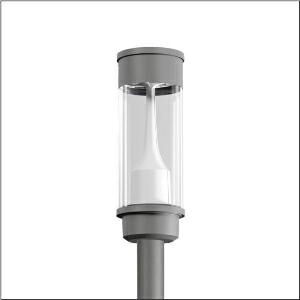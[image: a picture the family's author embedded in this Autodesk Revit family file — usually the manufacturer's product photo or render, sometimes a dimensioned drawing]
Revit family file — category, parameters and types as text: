
# Revit family: litepole_iq___pl1_2s_5xa5415cf14h_d917
name_source: partatom
category: Lighting Fixtures
units: mm (PartAtom-declared; Revit-internal decimal feet)

## family parameters
Cut with Voids When Loaded = No
Host = Face
Light Source = No
Part Type = Normal
Room Calculation Point = No
Round Connector Dimension = Use Diameter
Shared = No

## types (1)
- --- (1 x LED, 2970 lm, 23.9 W, 2200K)
    Apparent Load = 24 VA
    CIE Flux Codes = 23 62 94 96 100
    Color Rendering = 70
    Color Temperature = 2200K
    Default Elevation = 1800 mm
    Description = Litepole iQ, mast luminaire, Module 540 iQ-SR, primary light control with 3 zone facetted reflector, of plastic, silver coated, highly specular, structured, primary optical cover: cover, of PMMA, transparent, partly coated, light distribution: PL1.2s, light emission: direct distribution, primary light characteristic: symmetric, installation type: post-top, LED, High Power LED, rated luminous flux: 2.970lm, luminous efficacy: 124lm/W, light colour: 722, colour temperature: 2200K, control gear: ECG iQ, control: optimised constant luminous flux control (CLO 2.0), Desk-Remote (wireless, voltage-free reading and setting of iQ features in the workshop via application-optimized NFC function/RFID function), Light-Fading, Smart-Wire, Night-Set, Lumen-Switch, Temp-Guard, Auto-Match, Street-Remote, presetting dimming logarithmic, with terminal, 6-pole, max. 2.5mm², mains connection: 230..240V, AC, 50/60Hz, start of lifetime: 24W, end of service life: 26W, reduction: 12W, luminaire housing, upper part, of glass-fibre reinforced polyester, coated, Siteco® metallic grey (DB 702S), diameter: 210mm, height: 590mm, spigot size: d x l = 76 x 70mm (post-top) | with reducer (optional accessory) 60 x 70mm, post-top mast mounting element, of diecast aluminium, coated, Siteco® metallic grey (DB 702S), Module 540 iQ-SR, traffic white (RAL 9016), equipment: standard, protection rating (complete): IP65, insulation class (complete): insulation class II (safety insulation), certification: CE, ENEC, VDE, packaging unit: 1 piece

Light Distribution: PL1.2s
    Height = 590 mm
    Lamp = 1 x LED
    Lamp Light Flux = 2970 lm
    Lamp Power = 23.9 W
    Lamp count = 1
    Length = 220 mm
    Luminous efficacy = 124 lm/W
    Manufacturer = Siteco
    ModVariant = No
    Model = 5XA5415CF14H
    Number of Poles = 1
    OnlyDefault = Yes
    Power Factor = 1
    Product Name = Litepole iQ | PL1.2s
    Product group = mast luminaire | pylon top
    ProductGroupID = 6100
    Protection Class = Protection class II
    Protection Degree = IP 65
    RLX_Detail_Level = 1
    RLX_Emergency_Light_Flux = 0 lm
    RLX_Emergency_Type = 0
    RLX_Emergency_Type_DB = No
    RlxData = <blob elided: 40065 chars, md5=0433116e>
    Socket = socket
    Standby Power = 0 W
    System Light Flux = 2970 lm
    System Power = 24 W
    Type Comments = factory setting: luminous flux: 100 % | dim-lin: 254 | 499 mA
    Type Image = l_1006025.jpg
    URL = http://relux.com
    VarID = @adj_094359
    Voltage = 0 V
    Weight = 0.00 kg
    Width = 0 mm  [stored 0 ft]

note: [stored X ft] marks values corroborated as IEEE doubles in the binary element streams (Revit-internal decimal feet)

## geometry (parser evidence)
native form markers: Blend x4, Sweep x9
no freeform markers — native parametric forms only
